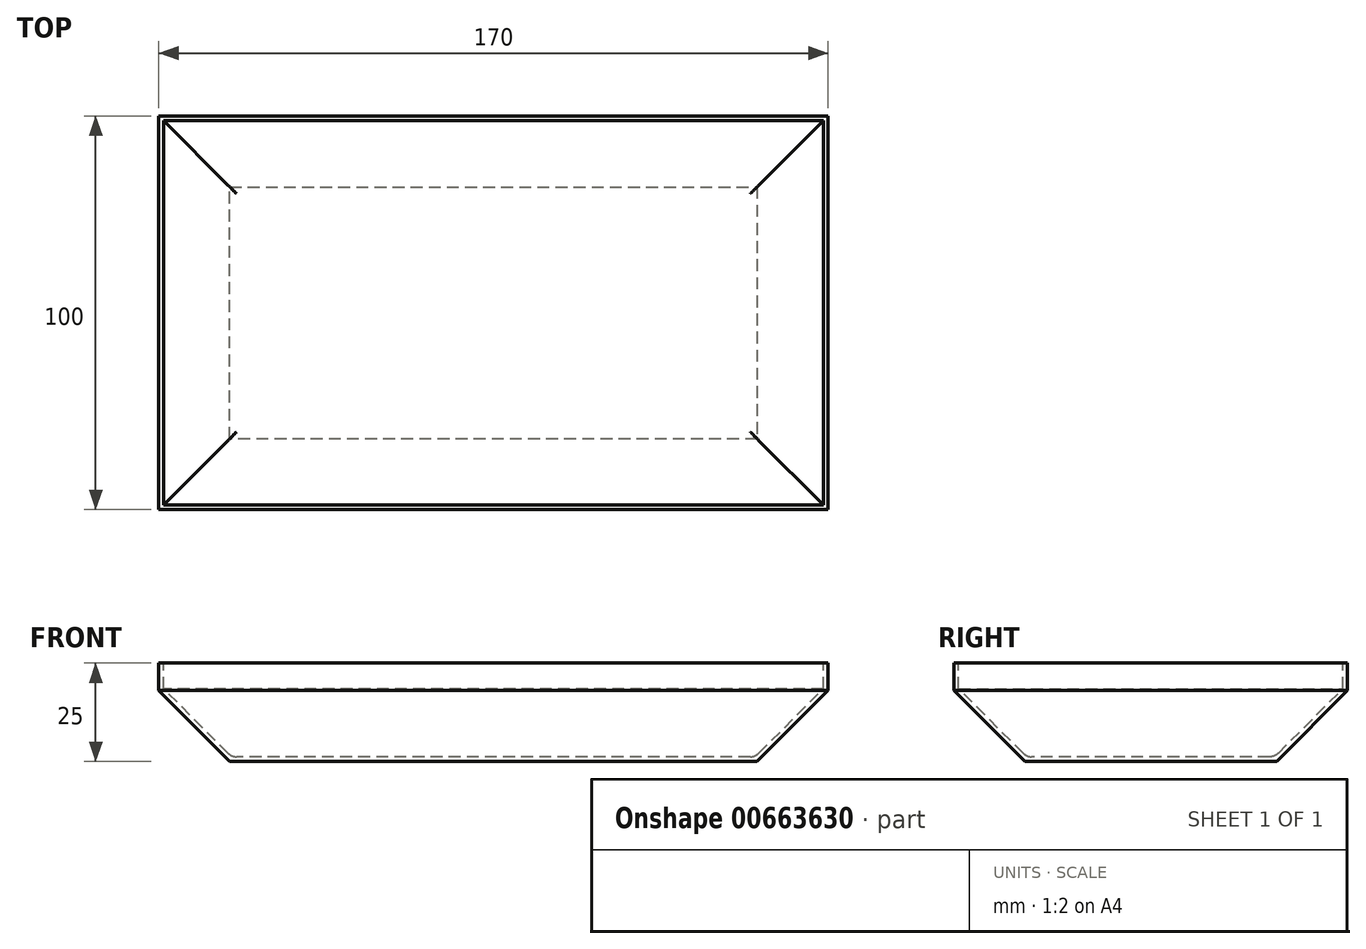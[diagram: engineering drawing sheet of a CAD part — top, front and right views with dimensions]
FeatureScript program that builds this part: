
annotation { "Feature Type Name" : "Feature", "Feature Type Description" : "" }
export const myFeature = defineFeature(function(context is Context, id is Id, definition is map)
    precondition{}
    {
        {
            var Q0;
            Q0=qCreatedBy(makeId("Top.planeOp"),FACE);
            cPlane(context, id + "F0", {"entities" : qUnion([Q0]), "cplaneType" : CPlaneType.OFFSET, "offset" : 25 * mm, "width" : 150 * mm, "height" : 150 * mm});
        }
        {
            var Q0;
            Q0=qCreatedBy(id+"F0.planeOp",FACE);
            var sketch = newSketch(context, id + "F1", { "sketchPlane" : qUnion([Q0])});
            skLineSegment(sketch, "E0.bottom", {"start": v(85, -100) * mm, "end": v(-85, -100) * mm});
            skLineSegment(sketch, "E0.top", {"start": v(85, 100) * mm, "end": v(-85, 100) * mm});
            skLineSegment(sketch, "E0.left", {"start": v(85, -100) * mm, "end": v(85, 100) * mm});
            skLineSegment(sketch, "E0.right", {"start": v(-85, -100) * mm, "end": v(-85, 100) * mm});
            skPoint(sketch, "E0.middle", {"position": v(0, 0) * mm});
            skLineSegment(sketch, "E1", {"start": v(-85, 0) * mm, "end": v(85, 0) * mm});
            skSolve(sketch);
        }
        {
            var Q0;
            Q0=makeQuery(id+"F1.imprint","IMPRINT",FACE,{"disambiguationData":[TD([[makeQuery(id+"F1.imprint","IMPRINT",EDGE,{"derivedFrom":sQuery(id+"F1.wireOp",EDGE,"E0.bottom")}),-1.0]])]});
            extrude(context, id + "F2", {"entities" : qUnion([Q0]), "oppositeDirection" : true, "depth" : 25 * mm, "offsetDistance" : 25 * mm});
        }
        {
            var Q0;
            Q0=makeQuery(id+"F2.opExtrude","CAP_FACE",FACE,{"disambiguationData":[OSD([sQuery(id+"F1.wireOp",EDGE,"E0.bottom"),sQuery(id+"F1.wireOp",EDGE,"E0.top"),sQuery(id+"F1.wireOp",EDGE,"E0.left"),sQuery(id+"F1.wireOp",EDGE,"E0.right")])],"isStart":false});
            chamfer(context, id + "F3", {"entities" : qUnion([Q0]), "width" : 18 * mm, "tangentPropagation" : true});
        }
        {
            var Q0;
            Q0=makeQuery(id+"F2.opExtrude","CAP_FACE",FACE,{"disambiguationData":[OSD([sQuery(id+"F1.wireOp",EDGE,"E0.bottom"),sQuery(id+"F1.wireOp",EDGE,"E0.top"),sQuery(id+"F1.wireOp",EDGE,"E0.left"),sQuery(id+"F1.wireOp",EDGE,"E0.right")])],"isStart":true});
            shell(context, id + "F4", {"entities" : qUnion([Q0]), "thickness" : 1.2 * mm});
        }
        {
            var Q0;
            Q0=makeQuery(id+"F4.opShell","OFFSET_FACE",FACE,{"disambiguationData":[OSD([sQuery(id+"F1.wireOp",EDGE,"E0.bottom"),sQuery(id+"F1.wireOp",EDGE,"E0.top"),sQuery(id+"F1.wireOp",EDGE,"E0.left"),sQuery(id+"F1.wireOp",EDGE,"E0.right")])]});
            fillet(context, id + "F5", {"entities" : qUnion([Q0]), "radius" : 3 * mm, "tangentPropagation" : true, "allowEdgeOverflow" : false});
        }
    });
